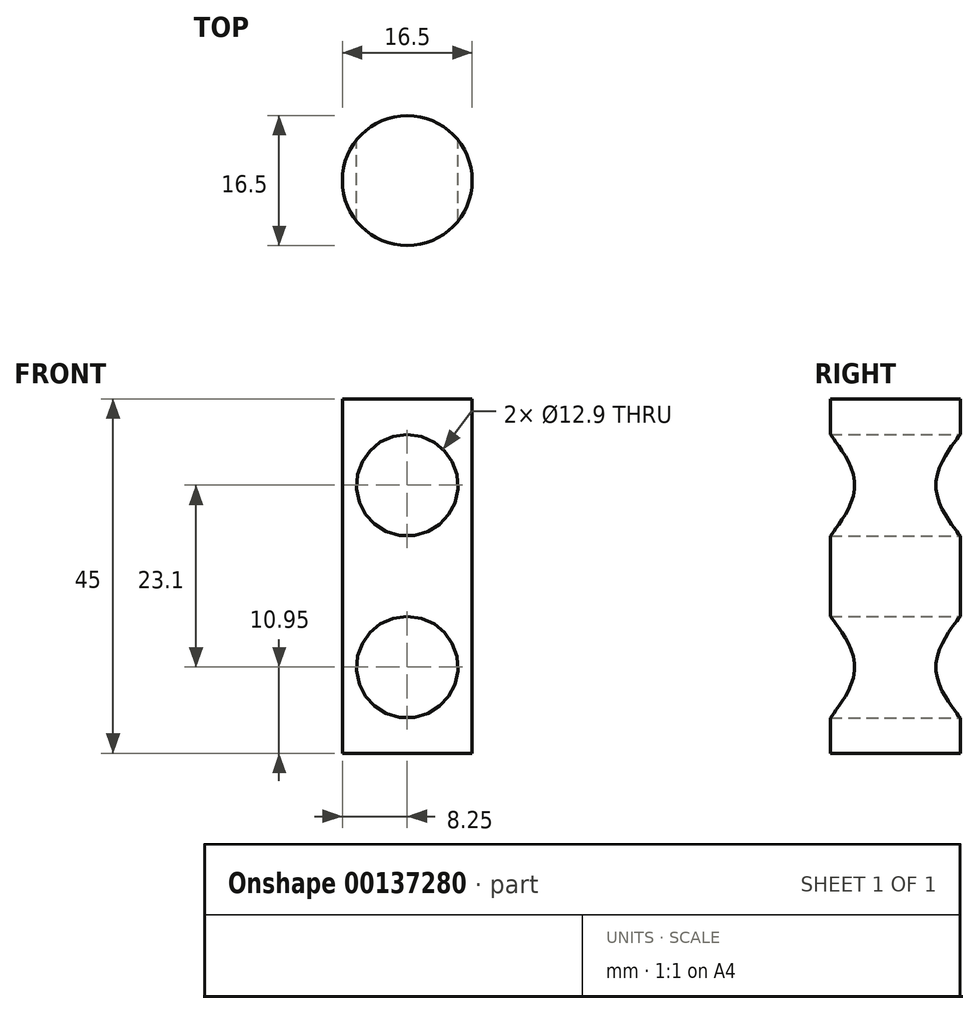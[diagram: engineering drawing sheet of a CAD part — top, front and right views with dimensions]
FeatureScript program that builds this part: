
annotation { "Feature Type Name" : "Feature", "Feature Type Description" : "" }
export const myFeature = defineFeature(function(context is Context, id is Id, definition is map)
    precondition{}
    {
        {
            var Q0;
            Q0=qCreatedBy(makeId("Top.planeOp"),FACE);
            var sketch = newSketch(context, id + "F0", { "sketchPlane" : qUnion([Q0])});
            skCircle(sketch, "E0", {"center": v(0, 0) * mm, "radius": 8.25 * mm});
            skSolve(sketch);
        }
        {
            var Q0;
            Q0 = qSketchRegion(id + "F0", true);
            var Q1;
            Q1=makeQuery(id+"F0.imprint","IMPRINT",FACE,{"disambiguationData":[TD([[makeQuery(id+"F0.imprint","IMPRINT",EDGE,{"derivedFrom":sQuery(id+"F0.wireOp",EDGE,"E0")}),1.0]])]});
            extrude(context, id + "F1", {"entities" : qUnion([Q0, Q1]), "depth" : 45 * mm});
        }
        {
            var Q0;
            Q0=qCreatedBy(makeId("Front.planeOp"),FACE);
            var sketch = newSketch(context, id + "F2", { "sketchPlane" : qUnion([Q0])});
            skLineSegment(sketch, "E1", {"start": v(0, 0) * mm, "end": v(0, 45) * mm, "construction": true});
            skCircle(sketch, "E2", {"center": v(0, 10.95) * mm, "radius": 6.45 * mm});
            skCircle(sketch, "E3", {"center": v(0, 34.05) * mm, "radius": 6.45 * mm});
            skSolve(sketch);
        }
        {
            var Q0;
            Q0 = qSketchRegion(id + "F2", true);
            extrude(context, id + "F3", {"entities" : qUnion([Q0]), "operationType" : NewBodyOperationType.REMOVE, "endBound" : BoundingType.SYMMETRIC, "depth" : 25 * mm});
        }
    });
